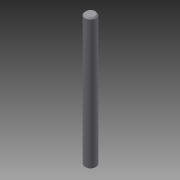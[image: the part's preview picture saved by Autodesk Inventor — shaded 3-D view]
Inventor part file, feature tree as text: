
AUTODESK INVENTOR PART (.ipt)
format: ipt  version: 2015 (Build 190159000, 159)  size: 83,968 bytes
history: native  units: in
note: dims shown in document units (in); Inventor stores cm internally (conversion verified against a paired STEP export)
features: other x3, extrude x1, chamfer x1, sketch x1
ambient origin geometry x8: Origin, YZ Plane, XZ Plane, XY Plane, X Axis, Y Axis, Z Axis, Center Point
bodies: Solid1 (feature_tree)
feature tree (6):
  other  "Axle-100mm - 739088.ipt"
  extrude  "Extrusion1"  Depth=0.3937in TaperAngle=0.0deg
  chamfer  "Chamfer1"  Distance=0.0197in Angle=45.0deg
  other  "tetrix_739088_2013::Axle-100mm - 739088.ipt"
  other  "TaggingFeature1"
  sketch  "Sketch1"  dims[d0=0.3937in d1=1.7717in d2=0.0in d3=0.0197in d4=0.125in d5=45.0deg]
